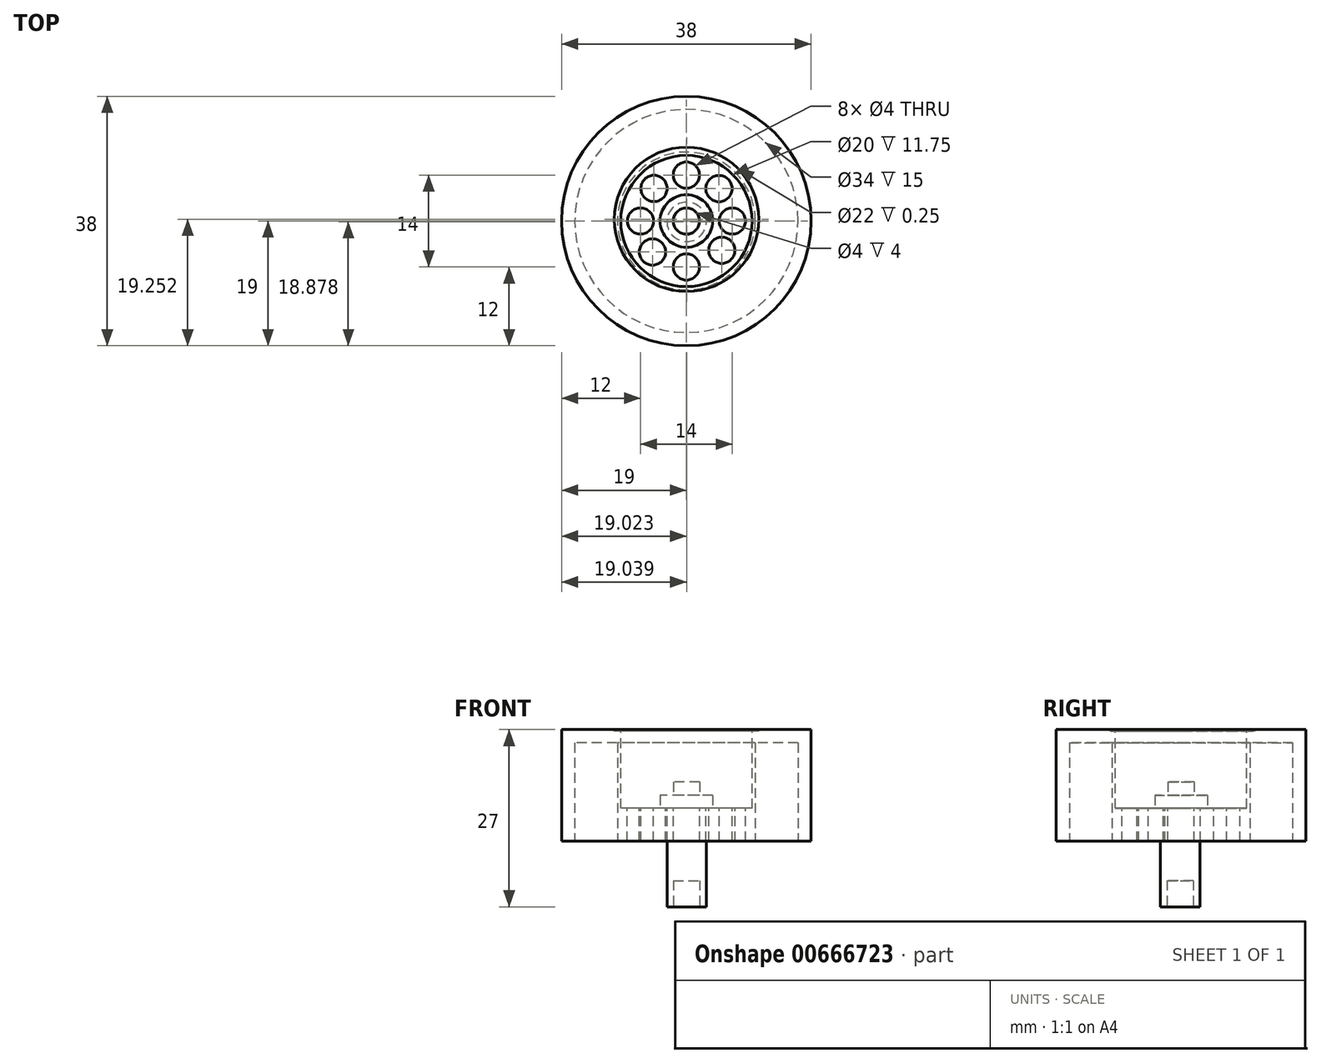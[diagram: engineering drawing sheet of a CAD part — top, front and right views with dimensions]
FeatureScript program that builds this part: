
annotation { "Feature Type Name" : "Feature", "Feature Type Description" : "" }
export const myFeature = defineFeature(function(context is Context, id is Id, definition is map)
    precondition{}
    {
        {
            var Q0;
            Q0=qCreatedBy(makeId("Top.planeOp"),FACE);
            var sketch = newSketch(context, id + "F0", { "sketchPlane" : qUnion([Q0])});
            skCircle(sketch, "E0", {"center": v(19, 19) * mm, "radius": 19 * mm});
            skSolve(sketch);
        }
        {
            var Q0;
            Q0=makeQuery(id+"F0.imprint","IMPRINT",FACE,{"disambiguationData":[TD([[makeQuery(id+"F0.imprint","IMPRINT",EDGE,{"derivedFrom":sQuery(id+"F0.wireOp",EDGE,"E0")}),1.0]])]});
            extrude(context, id + "F1", {"entities" : qUnion([Q0]), "depth" : 17 * mm, "offsetDistance" : 25 * mm});
        }
        {
            var Q0;
            Q0=qCreatedBy(makeId("Top.planeOp"),FACE);
            var sketch = newSketch(context, id + "F2", { "sketchPlane" : qUnion([Q0])});
            skLineSegment(sketch, "E1.right", {"start": v(19, 19) * mm, "end": v(19, 19) * mm});
            skCircle(sketch, "E2", {"center": v(19, 19) * mm, "radius": 17 * mm});
            skCircle(sketch, "E3", {"center": v(19, 19) * mm, "radius": 10.5 * mm});
            skSolve(sketch);
        }
        {
            var Q0;
            Q0=makeQuery(id+"F2.imprint","IMPRINT",FACE,{"disambiguationData":[TD([[makeQuery(id+"F2.imprint","IMPRINT",EDGE,{"derivedFrom":sQuery(id+"F2.wireOp",EDGE,"E2")}),1.0]])]});
            var Q1;
            Q1=sQuery(id+"F2.wireOp",EDGE,"E2");
            extrude(context, id + "F3", {"entities" : qUnion([Q0]), "operationType" : NewBodyOperationType.REMOVE, "surfaceEntities" : qUnion([Q1]), "depth" : 15 * mm, "offsetDistance" : 25 * mm});
        }
        {
            var Q0;
            Q0=makeQuery(id+"F0.imprint","IMPRINT",FACE,{"disambiguationData":[TD([[makeQuery(id+"F0.imprint","IMPRINT",EDGE,{"derivedFrom":sQuery(id+"F0.wireOp",EDGE,"E0")}),1.0]])]});
            var sketch = newSketch(context, id + "F4", { "sketchPlane" : qUnion([Q0])});
            skCircle(sketch, "E4", {"center": v(19.04, 18.88) * mm, "radius": 3 * mm});
            skSolve(sketch);
        }
        {
            var Q0;
            Q0=makeQuery(id+"F4.imprint","IMPRINT",FACE,{"disambiguationData":[TD([[makeQuery(id+"F4.imprint","IMPRINT",EDGE,{"derivedFrom":sQuery(id+"F4.wireOp",EDGE,"E4")}),1.0]])]});
            extrude(context, id + "F5", {"entities" : qUnion([Q0]), "operationType" : NewBodyOperationType.ADD, "oppositeDirection" : true, "depth" : 10 * mm, "offsetDistance" : 25 * mm});
        }
        {
            var Q0;
            Q0=makeQuery(id+"F1.opExtrude","CAP_FACE",FACE,{"disambiguationData":[OSD([sQuery(id+"F0.wireOp",EDGE,"E0")])],"isStart":false});
            var sketch = newSketch(context, id + "F6", { "sketchPlane" : qUnion([Q0])});
            skCircle(sketch, "E5", {"center": v(19, 19) * mm, "radius": 10 * mm});
            skSolve(sketch);
        }
        {
            var Q0;
            Q0=makeQuery(id+"F6.imprint","IMPRINT",FACE,{"disambiguationData":[TD([[makeQuery(id+"F6.imprint","IMPRINT",EDGE,{"derivedFrom":sQuery(id+"F6.wireOp",EDGE,"E5")}),1.0]])]});
            extrude(context, id + "F7", {"entities" : qUnion([Q0]), "operationType" : NewBodyOperationType.REMOVE, "oppositeDirection" : true, "depth" : 12 * mm, "offsetDistance" : 25 * mm});
        }
        {
            var Q0;
            Q0=makeQuery(id+"F7.boolean.opBoolean","COPY",FACE,{"derivedFrom":makeQuery(id+"F7.opExtrude","CAP_FACE",FACE,{"disambiguationData":[OSD([sQuery(id+"F6.wireOp",EDGE,"E5")])],"isStart":false})});
            var sketch = newSketch(context, id + "F8", { "sketchPlane" : qUnion([Q0])});
            skCircle(sketch, "E6", {"center": v(19, 19) * mm, "radius": 4 * mm});
            skCircle(sketch, "E7", {"center": v(19, 19) * mm, "radius": 2 * mm});
            skPoint(sketch, "E8.endSnap0", {"position": v(19, 24) * mm});
            skCircle(sketch, "E9", {"center": v(19, 26) * mm, "radius": 2 * mm});
            skCircle(sketch, "E10", {"center": v(23.96, 23.94) * mm, "radius": 2 * mm});
            skCircle(sketch, "E11", {"center": v(26, 19) * mm, "radius": 2 * mm});
            skCircle(sketch, "E12", {"center": v(24.4, 14.54) * mm, "radius": 2 * mm});
            skCircle(sketch, "E13", {"center": v(19, 12) * mm, "radius": 2 * mm});
            skCircle(sketch, "E14", {"center": v(13.84, 14.27) * mm, "radius": 2 * mm});
            skCircle(sketch, "E15", {"center": v(14.06, 23.96) * mm, "radius": 2 * mm});
            skCircle(sketch, "E16", {"center": v(12, 19) * mm, "radius": 2 * mm});
            skSolve(sketch);
        }
        {
            var Q0;
            Q0=makeQuery(id+"F8.imprint","IMPRINT",FACE,{"disambiguationData":[TD([[makeQuery(id+"F8.imprint","IMPRINT",EDGE,{"derivedFrom":sQuery(id+"F8.wireOp",EDGE,"E9")}),1.0]])]});
            var Q1;
            Q1=makeQuery(id+"F8.imprint","IMPRINT",FACE,{"disambiguationData":[TD([[makeQuery(id+"F8.imprint","IMPRINT",EDGE,{"derivedFrom":sQuery(id+"F8.wireOp",EDGE,"E10")}),1.0]])]});
            var Q2;
            Q2=makeQuery(id+"F8.imprint","IMPRINT",FACE,{"disambiguationData":[TD([[makeQuery(id+"F8.imprint","IMPRINT",EDGE,{"derivedFrom":sQuery(id+"F8.wireOp",EDGE,"E11")}),1.0]])]});
            var Q3;
            Q3=makeQuery(id+"F8.imprint","IMPRINT",FACE,{"disambiguationData":[TD([[makeQuery(id+"F8.imprint","IMPRINT",EDGE,{"derivedFrom":sQuery(id+"F8.wireOp",EDGE,"E12")}),1.0]])]});
            var Q4;
            Q4=makeQuery(id+"F8.imprint","IMPRINT",FACE,{"disambiguationData":[TD([[makeQuery(id+"F8.imprint","IMPRINT",EDGE,{"derivedFrom":sQuery(id+"F8.wireOp",EDGE,"E13")}),1.0]])]});
            var Q5;
            Q5=makeQuery(id+"F8.imprint","IMPRINT",FACE,{"disambiguationData":[TD([[makeQuery(id+"F8.imprint","IMPRINT",EDGE,{"derivedFrom":sQuery(id+"F8.wireOp",EDGE,"E14")}),1.0]])]});
            var Q6;
            Q6=makeQuery(id+"F8.imprint","IMPRINT",FACE,{"disambiguationData":[TD([[makeQuery(id+"F8.imprint","IMPRINT",EDGE,{"derivedFrom":sQuery(id+"F8.wireOp",EDGE,"E16")}),1.0]])]});
            var Q7;
            Q7=makeQuery(id+"F8.imprint","IMPRINT",FACE,{"disambiguationData":[TD([[makeQuery(id+"F8.imprint","IMPRINT",EDGE,{"derivedFrom":sQuery(id+"F8.wireOp",EDGE,"E15")}),1.0]])]});
            extrude(context, id + "F9", {"entities" : qUnion([Q0, Q1, Q2, Q3, Q4, Q5, Q6, Q7]), "operationType" : NewBodyOperationType.REMOVE, "oppositeDirection" : true, "depth" : 25 * mm, "offsetDistance" : 25 * mm});
        }
        {
            var Q0;
            Q0=makeQuery(id+"F8.imprint","IMPRINT",FACE,{"disambiguationData":[TD([[makeQuery(id+"F8.imprint","IMPRINT",EDGE,{"derivedFrom":sQuery(id+"F8.wireOp",EDGE,"E7")}),1.0]])]});
            extrude(context, id + "F10", {"entities" : qUnion([Q0]), "operationType" : NewBodyOperationType.ADD, "depth" : 4 * mm, "offsetDistance" : 25 * mm});
        }
        {
            var Q0;
            Q0=makeQuery(id+"F8.imprint","IMPRINT",FACE,{"disambiguationData":[TD([[makeQuery(id+"F8.imprint","IMPRINT",EDGE,{"derivedFrom":sQuery(id+"F8.wireOp",EDGE,"E6")}),1.0]])]});
            extrude(context, id + "F11", {"entities" : qUnion([Q0]), "operationType" : NewBodyOperationType.ADD, "depth" : 2 * mm, "offsetDistance" : 25 * mm});
        }
        {
            var Q0;
            Q0=makeQuery(id+"F1.opExtrude","CAP_FACE",FACE,{"disambiguationData":[OSD([sQuery(id+"F0.wireOp",EDGE,"E0")])],"isStart":false});
            var sketch = newSketch(context, id + "F12", { "sketchPlane" : qUnion([Q0])});
            skCircle(sketch, "E17", {"center": v(19.02, 19.25) * mm, "radius": 11 * mm});
            skSolve(sketch);
        }
        {
            var Q0;
            Q0=makeQuery(id+"F12.imprint","IMPRINT",FACE,{"disambiguationData":[TD([[makeQuery(id+"F12.imprint","IMPRINT",EDGE,{"derivedFrom":sQuery(id+"F12.wireOp",EDGE,"E17")}),1.0]])]});
            extrude(context, id + "F13", {"entities" : qUnion([Q0]), "operationType" : NewBodyOperationType.REMOVE, "oppositeDirection" : true, "depth" : .25 * mm, "offsetDistance" : 25 * mm});
        }
        {
            var Q0;
            Q0=makeQuery(id+"F5.opExtrude","CAP_FACE",FACE,{"disambiguationData":[OSD([sQuery(id+"F4.wireOp",EDGE,"E4")])],"isStart":false});
            var sketch = newSketch(context, id + "F14", { "sketchPlane" : qUnion([Q0])});
            skCircle(sketch, "E18", {"center": v(19.04, -18.88) * mm, "radius": 2 * mm});
            skSolve(sketch);
        }
        {
            var Q0;
            Q0=makeQuery(id+"F14.imprint","IMPRINT",FACE,{"disambiguationData":[TD([[makeQuery(id+"F14.imprint","IMPRINT",EDGE,{"derivedFrom":sQuery(id+"F14.wireOp",EDGE,"E18")}),1.0]])]});
            extrude(context, id + "F15", {"entities" : qUnion([Q0]), "operationType" : NewBodyOperationType.REMOVE, "oppositeDirection" : true, "depth" : 4 * mm, "offsetDistance" : 25 * mm});
        }
    });
